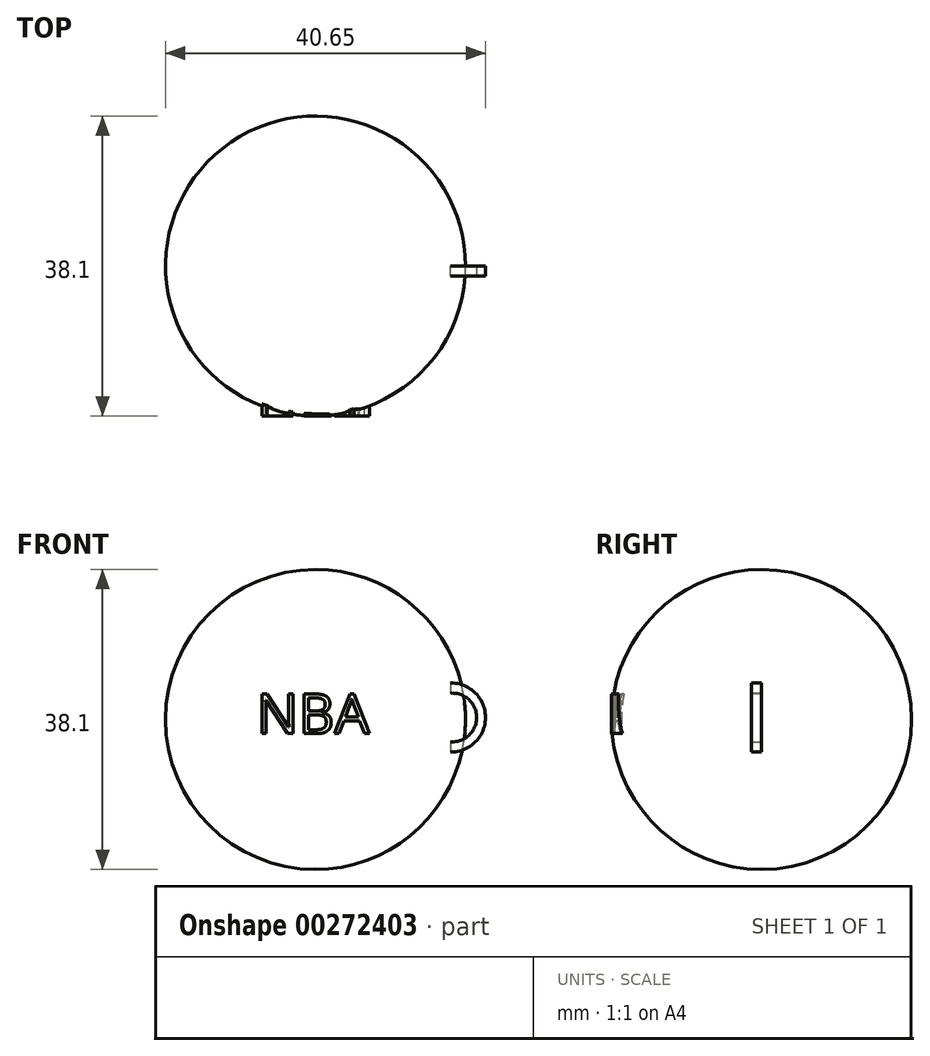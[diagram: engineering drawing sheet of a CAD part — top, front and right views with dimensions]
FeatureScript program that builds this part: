
annotation { "Feature Type Name" : "Feature", "Feature Type Description" : "" }
export const myFeature = defineFeature(function(context is Context, id is Id, definition is map)
    precondition{}
    {
        {
            var Q0;
            Q0=qCreatedBy(makeId("Front.planeOp"),FACE);
            var sketch = newSketch(context, id + "F0", { "sketchPlane" : qUnion([Q0])});
            skArc(sketch, "E0", {"start": v(0, -19.05) * mm, "mid": v(19.05, 0) * mm, "end": v(0, 19.05) * mm});
            skLineSegment(sketch, "E1", {"start": v(0, 19.05) * mm, "end": v(0, -19.05) * mm});
            skSolve(sketch);
        }
        {
            var Q0;
            Q0 = qSketchRegion(id + "F0", true);
            var Q1;
            Q1=sQuery(id+"F0.wireOp",EDGE,"E1");
            revolve(context, id + "F1", {"entities" : qUnion([Q0]), "axis" : qUnion([Q1]), "revolveType" : RevolveType.FULL});
        }
        {
            var Q0;
            Q0=qCreatedBy(makeId("Front.planeOp"),FACE);
            var sketch = newSketch(context, id + "F2", { "sketchPlane" : qUnion([Q0])});
            skPoint(sketch, "E2.center.orphan", {"position": v(17.18, 0) * mm});
            skArc(sketch, "E3", {"start": v(17.18, -4.13) * mm, "mid": v(21.6, 0.25) * mm, "end": v(17.18, 4.63) * mm});
            skArc(sketch, "E4", {"start": v(17.18, -2.83) * mm, "mid": v(20.48, 0.25) * mm, "end": v(17.18, 3.33) * mm});
            skLineSegment(sketch, "E5", {"start": v(17.18, 4.63) * mm, "end": v(17.18, 3.33) * mm});
            skLineSegment(sketch, "E6", {"start": v(17.18, -2.83) * mm, "end": v(17.18, -4.13) * mm});
            skSolve(sketch);
        }
        {
            var Q0;
            Q0 = qSketchRegion(id + "F2", true);
            extrude(context, id + "F3", {"entities" : qUnion([Q0]), "depth" : 1.27 * mm});
        }
        {
            var Q0;
            Q0=qCreatedBy(makeId("Front.planeOp"),FACE);
            var sketch = newSketch(context, id + "F4", { "sketchPlane" : qUnion([Q0])});
            skText(sketch, "E7", { "text": "NBA", "fontName": "OpenSans-Regular.ttf"});
            const initialGuessF4  = {"E7": [-0.0075, -0.0018, 1, 0, 0.00508]};
            skSetInitialGuess(sketch, initialGuessF4);
            skSolve(sketch);
        }
        {
            var Q0;
            Q0 = qSketchRegion(id + "F4", true);
            extrude(context, id + "F5", {"entities" : qUnion([Q0]), "operationType" : NewBodyOperationType.ADD, "depth" : 19.05 * mm});
        }
    });
